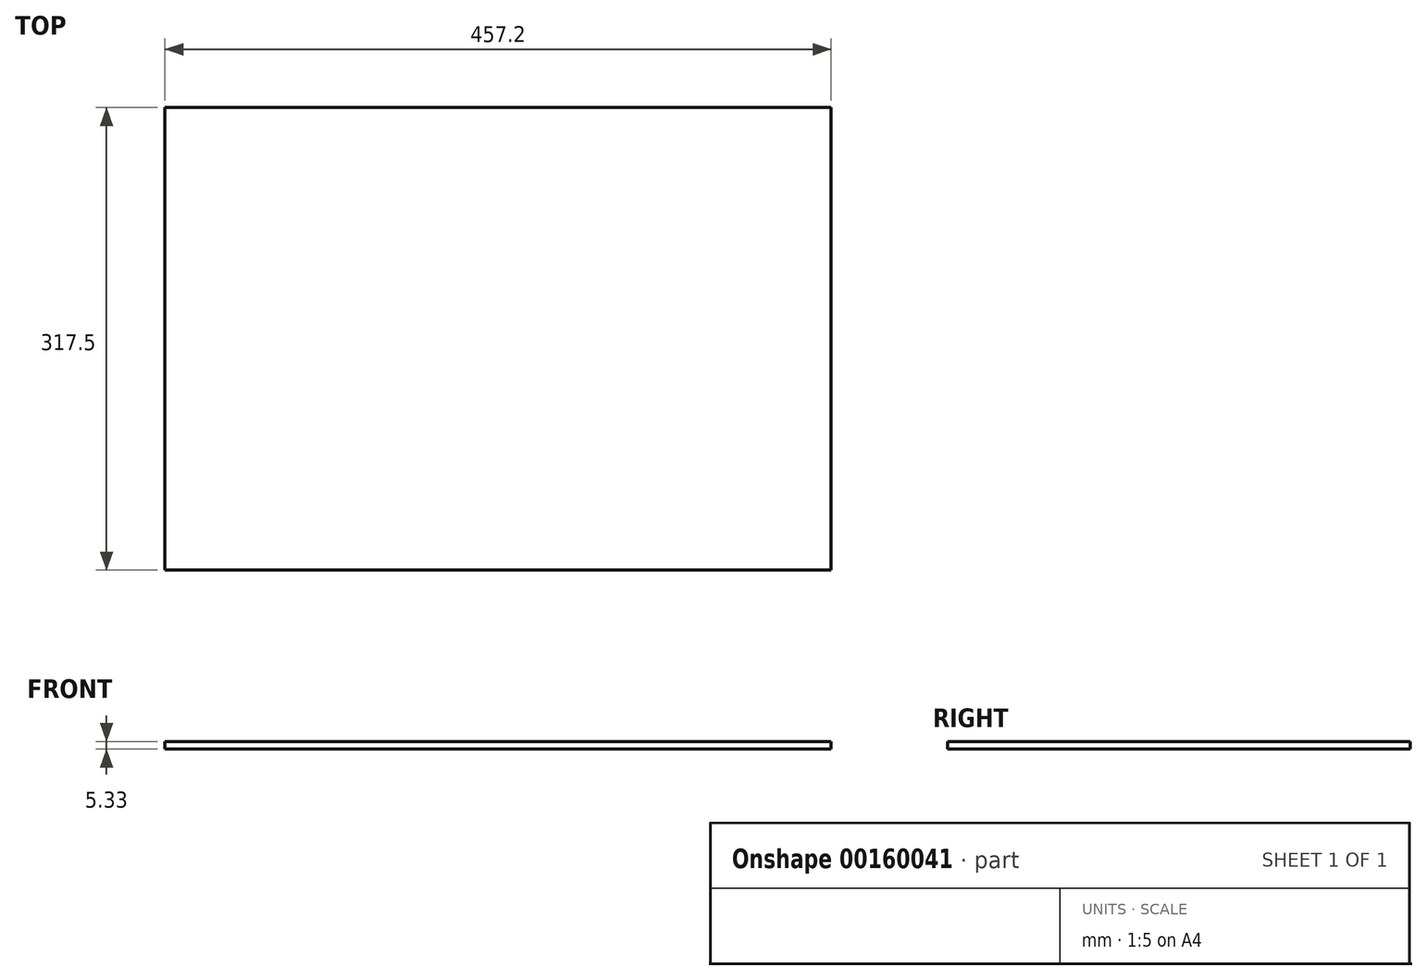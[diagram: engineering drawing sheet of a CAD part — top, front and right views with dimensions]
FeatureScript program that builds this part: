
annotation { "Feature Type Name" : "Feature", "Feature Type Description" : "" }
export const myFeature = defineFeature(function(context is Context, id is Id, definition is map)
    precondition{}
    {
        {
            var Q0;
            Q0=qCreatedBy(makeId("Top.planeOp"),FACE);
            var sketch = newSketch(context, id + "F0", { "sketchPlane" : qUnion([Q0])});
            skLineSegment(sketch, "E0.bottom", {"start": v(-337.3, 154.13) * mm, "end": v(119.9, 154.13) * mm});
            skLineSegment(sketch, "E0.top", {"start": v(-337.3, -163.37) * mm, "end": v(119.9, -163.37) * mm});
            skLineSegment(sketch, "E0.left", {"start": v(-337.3, 154.13) * mm, "end": v(-337.3, -163.37) * mm});
            skLineSegment(sketch, "E0.right", {"start": v(119.9, 154.13) * mm, "end": v(119.9, -163.37) * mm});
            skSolve(sketch);
        }
        {
            var Q0;
            Q0 = qSketchRegion(id + "F0", true);
            extrude(context, id + "F1", {"entities" : qUnion([Q0]), "depth" : 5.33 * mm});
        }
    });
